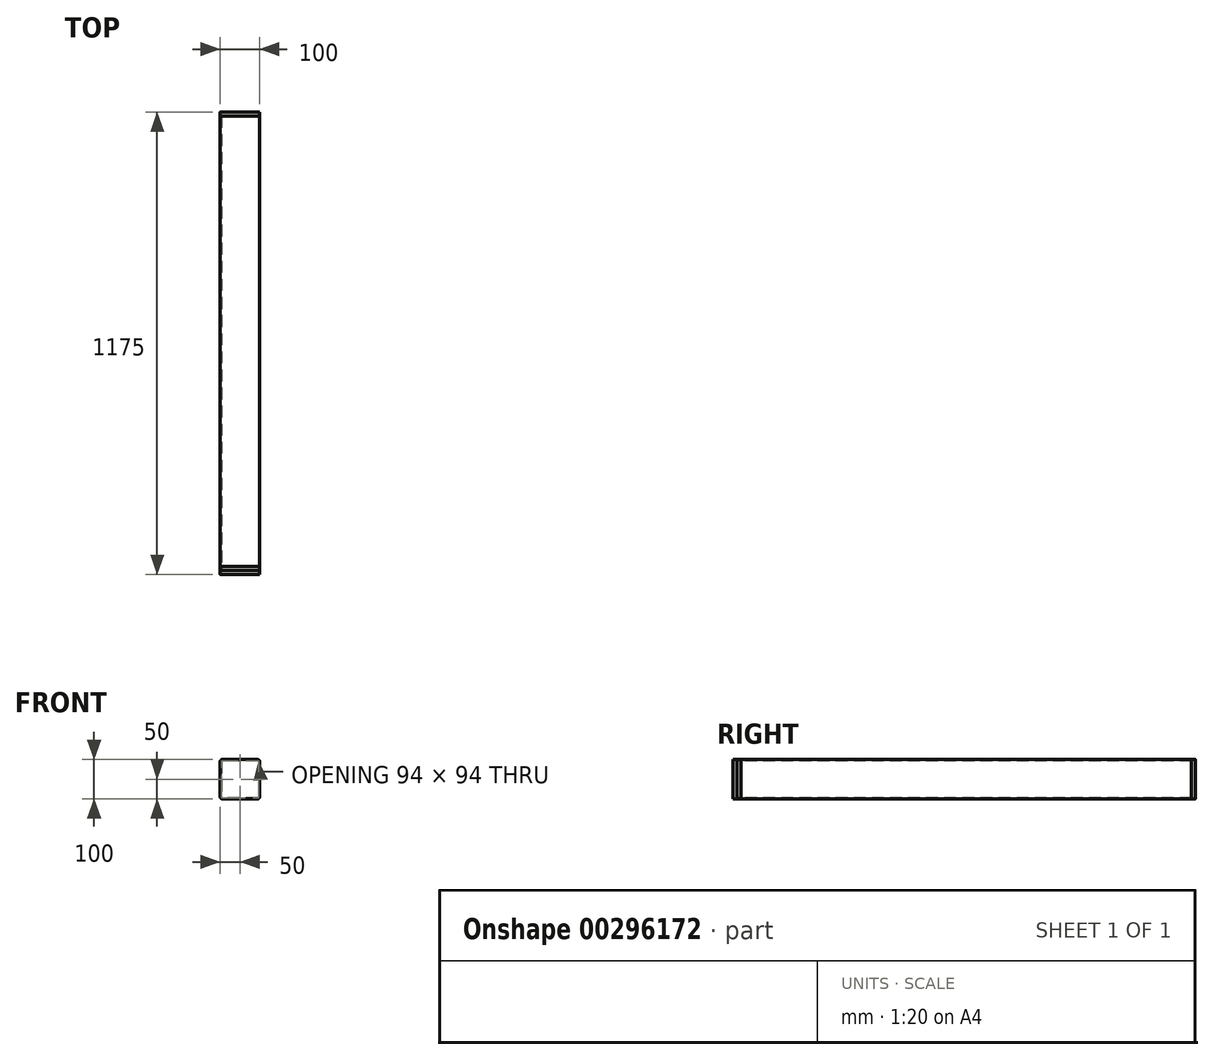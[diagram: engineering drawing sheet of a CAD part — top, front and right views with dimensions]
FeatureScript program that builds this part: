
annotation { "Feature Type Name" : "Feature", "Feature Type Description" : "" }
export const myFeature = defineFeature(function(context is Context, id is Id, definition is map)
    precondition{}
    {
        {
            var Q0;
            Q0=qCreatedBy(makeId("Front.planeOp"),FACE);
            var sketch = newSketch(context, id + "F0", { "sketchPlane" : qUnion([Q0])});
            skLineSegment(sketch, "E0.bottom", {"start": v(45, 50) * mm, "end": v(-45, 50) * mm});
            skLineSegment(sketch, "E0.top", {"start": v(45, -50) * mm, "end": v(-45, -50) * mm});
            skLineSegment(sketch, "E0.left", {"start": v(50, 45) * mm, "end": v(50, -45) * mm});
            skLineSegment(sketch, "E0.right", {"start": v(-50, 45) * mm, "end": v(-50, -45) * mm});
            skPoint(sketch, "E0.middle", {"position": v(0, 0) * mm});
            skPoint(sketch, "E1.visualSharp", {"position": v(-50, 50) * mm});
            skArc(sketch, "E1.filletArc", {"start": v(-45, 50) * mm, "mid": v(-48.54, 48.54) * mm, "end": v(-50, 45) * mm});
            skPoint(sketch, "E2.visualSharp", {"position": v(50, 50) * mm});
            skArc(sketch, "E2.filletArc", {"start": v(50, 45) * mm, "mid": v(48.54, 48.54) * mm, "end": v(45, 50) * mm});
            skPoint(sketch, "E3.visualSharp", {"position": v(50, -50) * mm});
            skArc(sketch, "E3.filletArc", {"start": v(45, -50) * mm, "mid": v(48.54, -48.54) * mm, "end": v(50, -45) * mm});
            skPoint(sketch, "E4.visualSharp", {"position": v(-50, -50) * mm});
            skArc(sketch, "E4.filletArc", {"start": v(-50, -45) * mm, "mid": v(-48.54, -48.54) * mm, "end": v(-45, -50) * mm});
            skArc(sketch, "E5.0", {"start": v(-45, 47) * mm, "mid": v(-46.41, 46.41) * mm, "end": v(-47, 45) * mm});
            skLineSegment(sketch, "E5.1", {"start": v(45, 47) * mm, "end": v(-45, 47) * mm});
            skLineSegment(sketch, "E5.2", {"start": v(-47, 45) * mm, "end": v(-47, -45) * mm});
            skArc(sketch, "E5.3", {"start": v(47, 45) * mm, "mid": v(46.41, 46.41) * mm, "end": v(45, 47) * mm});
            skArc(sketch, "E5.4", {"start": v(-47, -45) * mm, "mid": v(-46.41, -46.41) * mm, "end": v(-45, -47) * mm});
            skLineSegment(sketch, "E5.5", {"start": v(45, -47) * mm, "end": v(-45, -47) * mm});
            skArc(sketch, "E5.6", {"start": v(45, -47) * mm, "mid": v(46.41, -46.41) * mm, "end": v(47, -45) * mm});
            skLineSegment(sketch, "E5.7", {"start": v(47, 45) * mm, "end": v(47, -45) * mm});
            skSolve(sketch);
        }
        {
            var Q0;
            Q0=makeQuery(id+"F0.imprint","IMPRINT",FACE,{"disambiguationData":[TD([[makeQuery(id+"F0.imprint","IMPRINT",EDGE,{"derivedFrom":sQuery(id+"F0.wireOp",EDGE,"E0.bottom")}),1.0]])]});
            extrude(context, id + "F1", {"entities" : qUnion([Q0]), "oppositeDirection" : true, "depth" : (800 + 100 + 75 * 1 - 2 * 10 + 100 * 2) * mm});
        }
        {
            var Q0;
            Q0=makeQuery(id+"F1.opExtrude","CAP_FACE",FACE,{"disambiguationData":[OSD([sQuery(id+"F0.wireOp",EDGE,"E0.bottom"),sQuery(id+"F0.wireOp",EDGE,"E0.top"),sQuery(id+"F0.wireOp",EDGE,"E0.left"),sQuery(id+"F0.wireOp",EDGE,"E0.right"),sQuery(id+"F0.wireOp",EDGE,"E1.filletArc"),sQuery(id+"F0.wireOp",EDGE,"E2.filletArc"),sQuery(id+"F0.wireOp",EDGE,"E3.filletArc"),sQuery(id+"F0.wireOp",EDGE,"E4.filletArc"),sQuery(id+"F0.wireOp",EDGE,"E5.0"),sQuery(id+"F0.wireOp",EDGE,"E5.1"),sQuery(id+"F0.wireOp",EDGE,"E5.2"),sQuery(id+"F0.wireOp",EDGE,"E5.3"),sQuery(id+"F0.wireOp",EDGE,"E5.4"),sQuery(id+"F0.wireOp",EDGE,"E5.5"),sQuery(id+"F0.wireOp",EDGE,"E5.6"),sQuery(id+"F0.wireOp",EDGE,"E5.7")])],"isStart":true});
            cPlane(context, id + "F2", {"entities" : qUnion([Q0]), "cplaneType" : CPlaneType.OFFSET, "offset" : 10 * mm, "width" : 150 * mm, "height" : 150 * mm});
        }
        {
            var Q0;
            Q0=qCreatedBy(id+"F2.planeOp",FACE);
            var sketch = newSketch(context, id + "F3", { "sketchPlane" : qUnion([Q0])});
            skLineSegment(sketch, "E6.bottom", {"start": v(-45, 50) * mm, "end": v(45, 50) * mm});
            skLineSegment(sketch, "E6.top", {"start": v(-45, -50) * mm, "end": v(45, -50) * mm});
            skLineSegment(sketch, "E6.left", {"start": v(-50, 45) * mm, "end": v(-50, -45) * mm});
            skLineSegment(sketch, "E6.right", {"start": v(50, 45) * mm, "end": v(50, -45) * mm});
            skPoint(sketch, "E6.middle", {"position": v(0, 0) * mm});
            skPoint(sketch, "E7.visualSharp", {"position": v(-50, 50) * mm});
            skArc(sketch, "E7.filletArc", {"start": v(-45, 50) * mm, "mid": v(-48.54, 48.54) * mm, "end": v(-50, 45) * mm});
            skPoint(sketch, "E8.visualSharp", {"position": v(50, 50) * mm});
            skArc(sketch, "E8.filletArc", {"start": v(50, 45) * mm, "mid": v(48.54, 48.54) * mm, "end": v(45, 50) * mm});
            skPoint(sketch, "E9.visualSharp", {"position": v(50, -50) * mm});
            skArc(sketch, "E9.filletArc", {"start": v(45, -50) * mm, "mid": v(48.54, -48.54) * mm, "end": v(50, -45) * mm});
            skPoint(sketch, "E10.visualSharp", {"position": v(-50, -50) * mm});
            skArc(sketch, "E10.filletArc", {"start": v(-50, -45) * mm, "mid": v(-48.54, -48.54) * mm, "end": v(-45, -50) * mm});
            skSolve(sketch);
        }
        {
            var Q0;
            Q0=makeQuery(id+"F3.imprint","IMPRINT",FACE,{"disambiguationData":[TD([[makeQuery(id+"F3.imprint","IMPRINT",EDGE,{"derivedFrom":sQuery(id+"F3.wireOp",EDGE,"E6.bottom")}),-1.0]])]});
            extrude(context, id + "F4", {"entities" : qUnion([Q0]), "oppositeDirection" : true, "depth" : 20 * mm});
        }
        {
            var Q0;
            Q0=makeQuery(id+"F1.opExtrude","CAP_FACE",FACE,{"disambiguationData":[OSD([sQuery(id+"F0.wireOp",EDGE,"E0.bottom"),sQuery(id+"F0.wireOp",EDGE,"E0.top"),sQuery(id+"F0.wireOp",EDGE,"E0.left"),sQuery(id+"F0.wireOp",EDGE,"E0.right"),sQuery(id+"F0.wireOp",EDGE,"E1.filletArc"),sQuery(id+"F0.wireOp",EDGE,"E2.filletArc"),sQuery(id+"F0.wireOp",EDGE,"E3.filletArc"),sQuery(id+"F0.wireOp",EDGE,"E4.filletArc"),sQuery(id+"F0.wireOp",EDGE,"E5.0"),sQuery(id+"F0.wireOp",EDGE,"E5.1"),sQuery(id+"F0.wireOp",EDGE,"E5.2"),sQuery(id+"F0.wireOp",EDGE,"E5.3"),sQuery(id+"F0.wireOp",EDGE,"E5.4"),sQuery(id+"F0.wireOp",EDGE,"E5.5"),sQuery(id+"F0.wireOp",EDGE,"E5.6"),sQuery(id+"F0.wireOp",EDGE,"E5.7")])],"isStart":false});
            cPlane(context, id + "F5", {"entities" : qUnion([Q0]), "cplaneType" : CPlaneType.OFFSET, "offset" : 10 * mm, "width" : 150 * mm, "height" : 150 * mm});
        }
        {
            var Q0;
            Q0=qCreatedBy(id+"F5.planeOp",FACE);
            var sketch = newSketch(context, id + "F6", { "sketchPlane" : qUnion([Q0])});
            skLineSegment(sketch, "E11.bottom", {"start": v(-45, 50) * mm, "end": v(45, 50) * mm});
            skLineSegment(sketch, "E11.top", {"start": v(-45, -50) * mm, "end": v(45, -50) * mm});
            skLineSegment(sketch, "E11.left", {"start": v(-50, 45) * mm, "end": v(-50, -45) * mm});
            skLineSegment(sketch, "E11.right", {"start": v(50, 45) * mm, "end": v(50, -45) * mm});
            skPoint(sketch, "E11.middle", {"position": v(0, 0) * mm});
            skPoint(sketch, "E12.visualSharp", {"position": v(-50, 50) * mm});
            skArc(sketch, "E12.filletArc", {"start": v(-45, 50) * mm, "mid": v(-48.54, 48.54) * mm, "end": v(-50, 45) * mm});
            skPoint(sketch, "E13.visualSharp", {"position": v(50, 50) * mm});
            skArc(sketch, "E13.filletArc", {"start": v(50, 45) * mm, "mid": v(48.54, 48.54) * mm, "end": v(45, 50) * mm});
            skPoint(sketch, "E14.visualSharp", {"position": v(50, -50) * mm});
            skArc(sketch, "E14.filletArc", {"start": v(45, -50) * mm, "mid": v(48.54, -48.54) * mm, "end": v(50, -45) * mm});
            skPoint(sketch, "E15.visualSharp", {"position": v(-50, -50) * mm});
            skArc(sketch, "E15.filletArc", {"start": v(-50, -45) * mm, "mid": v(-48.54, -48.54) * mm, "end": v(-45, -50) * mm});
            skSolve(sketch);
        }
        {
            var Q0;
            Q0=makeQuery(id+"F6.imprint","IMPRINT",FACE,{"disambiguationData":[TD([[makeQuery(id+"F6.imprint","IMPRINT",EDGE,{"derivedFrom":sQuery(id+"F6.wireOp",EDGE,"E11.bottom")}),-1.0]])]});
            extrude(context, id + "F7", {"entities" : qUnion([Q0]), "oppositeDirection" : true, "depth" : 10 * mm});
        }
    });
